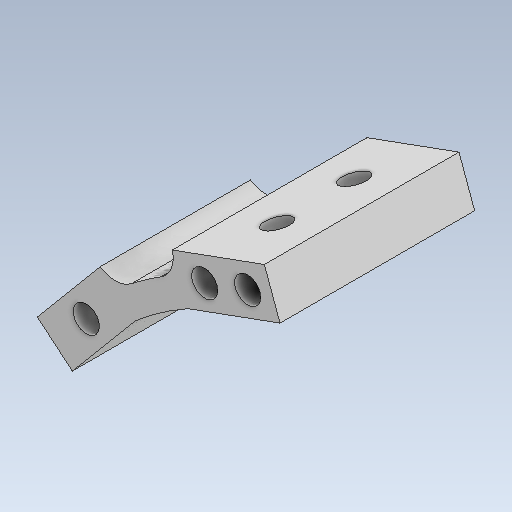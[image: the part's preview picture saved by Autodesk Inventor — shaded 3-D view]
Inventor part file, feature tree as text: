
AUTODESK INVENTOR PART (.ipt)
format: ipt  version: 2020 (Build 240168000, 168)  size: 286,720 bytes
history: native  units: mm
features: reference x9, other x8, sketch x7, extrude x7, projected_geometry x6, fillet x2, plane x1
ambient origin geometry x8: Origin, YZ Plane, XZ Plane, XY Plane, X Axis, Y Axis, Z Axis, Center Point
bodies: Solid1 (feature_tree)
feature tree (40):
  sketch  "Sketch1"  dims[d0=47.0mm d1=6.981317mm]
  plane  "Work Plane1"
  extrude  "Extrusion1"  Depth=6.981317mm
  extrude  "Extrusion2"  Depth=7.0mm
  extrude  "Extrusion3"  Depth=47.0mm
  extrude  "Extrusion4"  Depth=3.5mm
  extrude  "Extrusion5"  Depth=4.0mm
  fillet  "Fillet1"  Radius=48.5mm
  fillet  "Fillet2"  Radius=4.0mm
  extrude  "Extrusion6"  Depth=4.0mm
  extrude  "Extrusion7"  Depth=4.0mm
  reference  "Reference1"
  reference  "Reference2"
  reference  "Reference3"
  reference  "Reference4"
  reference  "Reference5"
  reference  "Reference6"
  sketch  "Sketch2"  dims[d2=3.5mm d3=7.0mm]
  reference  "Reference7"
  sketch  "Sketch3"  dims[d4=15.0mm d5=47.0mm]
  sketch  "Sketch4"  dims[d6=30.0deg d7=3.5mm]
  reference  "Reference8"
  projected_geometry  "Projected Loop1"
  projected_geometry  "Projected Loop2"
  projected_geometry  "Projected Loop3"
  sketch  "Sketch5"  dims[d8=7.0mm d9=15.0mm d10=48.5mm d11=4.0mm]
  projected_geometry  "Projected Loop4"
  sketch  "Sketch6"  dims[d12=4.0mm d13=52.5mm]
  reference  "Reference9"
  projected_geometry  "Projected Loop5"
  sketch  "Sketch7"  dims[d14=10.0mm d15=0.0mm d16=4.0mm d17=4.0mm d18=7.0mm d19=0.0mm d20=7.0mm d21=0.0mm d22=100.0mm d23=0.0mm d24=7.5mm d25=4.0mm d26=7.0mm d27=0.0mm d28=4.0mm d29=7.0mm d30=7.0mm d31=2.0mm d32=7.0mm d33=2.0mm d34=4.0mm d35=4.0mm d36=7.0mm d37=0.0mm d38=5.0mm d39=5.0mm d40=4.0mm d41=4.0mm d42=7.0mm d43=0.0mm]
  projected_geometry  "Projected Loop6"
  parser-record x1  (decoder bookkeeping rows leaked as tree rows — omitted from the tree; the rows remain in map.json)
  other  "reducer_1.iam"
  other  "motor_holder_2:1"
  other  "xl_20:1"
  other  "motor_holder_1:1"
  other  "90_motor:1"
  other  "90motor_top:1"
  other  "90motor_base:1"
note: 1 file-system path scrubbed to <path> (originals preserved in map.json)
